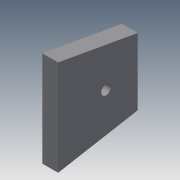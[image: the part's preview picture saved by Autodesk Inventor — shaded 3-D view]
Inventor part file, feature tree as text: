
AUTODESK INVENTOR PART (.ipt)
format: ipt  version: 2013 (Build 170138000, 138)  size: 67,584 bytes
history: native  units: mm
features: extrude x1, sketch x1
ambient origin geometry x8: Origin, YZ Plane, XZ Plane, XY Plane, X Axis, Y Axis, Z Axis, Center Point
bodies: Solid1 (feature_tree)
feature tree (2):
  extrude  "Extrusion1"  [1 undecoded]
  sketch  "Sketch1"  dims[d7=10.0mm d8=0.0mm]
note: 1 required parameter value undecoded (feature->parameter linkage not recoverable at this tier; creation-order binding heuristic only, values carry confidence <= 0.55)
